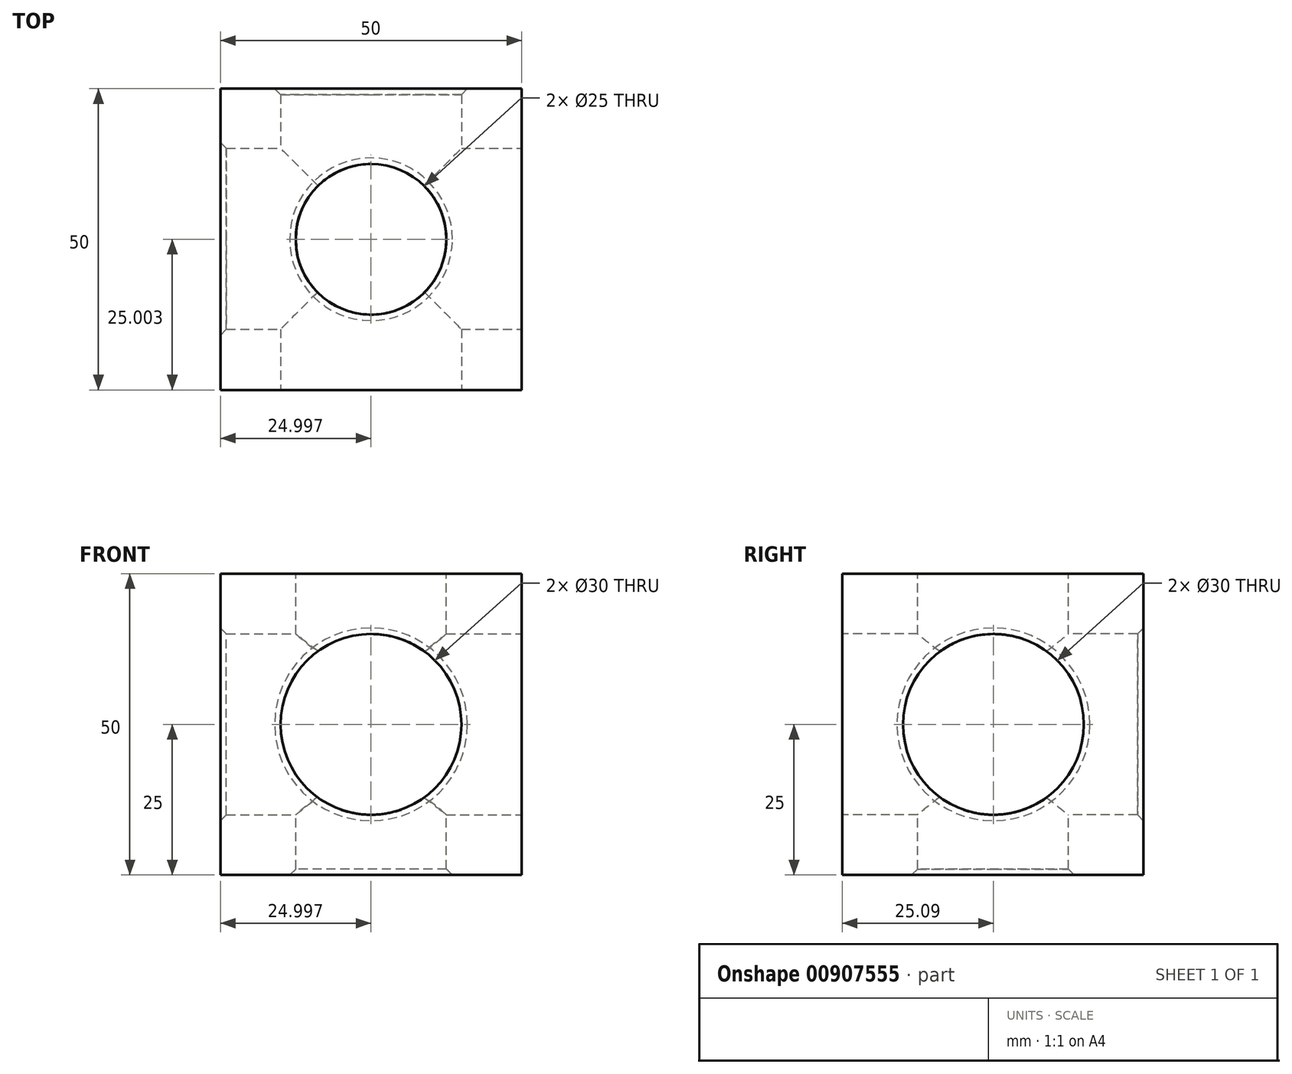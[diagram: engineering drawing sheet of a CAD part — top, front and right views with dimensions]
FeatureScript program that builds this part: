
annotation { "Feature Type Name" : "Feature", "Feature Type Description" : "" }
export const myFeature = defineFeature(function(context is Context, id is Id, definition is map)
    precondition{}
    {
        {
            var Q0;
            Q0=qCreatedBy(makeId("Top.planeOp"),FACE);
            var sketch = newSketch(context, id + "F0", { "sketchPlane" : qUnion([Q0])});
            skLineSegment(sketch, "E0.bottom", {"start": v(-87.73, 24.91) * mm, "end": v(-37.73, 24.91) * mm});
            skLineSegment(sketch, "E0.top", {"start": v(-87.73, -25.09) * mm, "end": v(-37.73, -25.09) * mm});
            skLineSegment(sketch, "E0.left", {"start": v(-87.73, 24.91) * mm, "end": v(-87.73, -25.09) * mm});
            skLineSegment(sketch, "E0.right", {"start": v(-37.73, 24.91) * mm, "end": v(-37.73, -25.09) * mm});
            skSolve(sketch);
        }
        {
            var Q0;
            Q0=makeQuery(id+"F0.imprint","IMPRINT",FACE,{"disambiguationData":[TD([[makeQuery(id+"F0.imprint","IMPRINT",EDGE,{"derivedFrom":sQuery(id+"F0.wireOp",EDGE,"E0.bottom")}),-1.0]])]});
            extrude(context, id + "F1", {"entities" : qUnion([Q0]), "depth" : 50 * mm, "offsetDistance" : 25 * mm});
        }
        {
            var Q0;
            Q0=makeQuery(id+"F1.opExtrude","SWEPT_FACE",FACE,{"disambiguationData":[OSD([sQuery(id+"F0.wireOp",EDGE,"E0.top")])]});
            var sketch = newSketch(context, id + "F2", { "sketchPlane" : qUnion([Q0])});
            skCircle(sketch, "E1", {"center": v(-62.73, 25) * mm, "radius": 15 * mm});
            skPoint(sketch, "E1.centerSnap0", {"position": v(-87.73, 25) * mm});
            skPoint(sketch, "E1.centerSnap1", {"position": v(-62.73, 50) * mm});
            skSolve(sketch);
        }
        {
            var Q0;
            Q0=makeQuery(id+"F2.imprint","IMPRINT",FACE,{"disambiguationData":[TD([[makeQuery(id+"F2.imprint","IMPRINT",EDGE,{"derivedFrom":sQuery(id+"F2.wireOp",EDGE,"E1")}),1.0]])]});
            extrude(context, id + "F3", {"entities" : qUnion([Q0]), "operationType" : NewBodyOperationType.REMOVE, "endBound" : BoundingType.THROUGH_ALL, "oppositeDirection" : true, "depth" : 25 * mm, "offsetDistance" : 25 * mm});
        }
        {
            var Q0;
            Q0=makeQuery(id+"F1.opExtrude","SWEPT_FACE",FACE,{"disambiguationData":[OSD([sQuery(id+"F0.wireOp",EDGE,"E0.right")])]});
            var sketch = newSketch(context, id + "F4", { "sketchPlane" : qUnion([Q0])});
            skCircle(sketch, "E2", {"center": v(0, 25) * mm, "radius": 15 * mm});
            skPoint(sketch, "E2.centerSnap0", {"position": v(-25.09, 25) * mm});
            skSolve(sketch);
        }
        {
            var Q0;
            Q0=makeQuery(id+"F4.imprint","IMPRINT",FACE,{"disambiguationData":[TD([[makeQuery(id+"F4.imprint","IMPRINT",EDGE,{"derivedFrom":sQuery(id+"F4.wireOp",EDGE,"E2")}),1.0]])]});
            extrude(context, id + "F5", {"entities" : qUnion([Q0]), "operationType" : NewBodyOperationType.REMOVE, "endBound" : BoundingType.THROUGH_ALL, "oppositeDirection" : true, "depth" : 25 * mm, "offsetDistance" : 25 * mm});
        }
        {
            var Q0;
            Q0=makeQuery(id+"F1.opExtrude","CAP_FACE",FACE,{"disambiguationData":[OSD([sQuery(id+"F0.wireOp",EDGE,"E0.bottom"),sQuery(id+"F0.wireOp",EDGE,"E0.top"),sQuery(id+"F0.wireOp",EDGE,"E0.left"),sQuery(id+"F0.wireOp",EDGE,"E0.right")])],"isStart":false});
            var sketch = newSketch(context, id + "F6", { "sketchPlane" : qUnion([Q0])});
            skCircle(sketch, "E3", {"center": v(-62.73, -0.09) * mm, "radius": 12.5 * mm});
            skPoint(sketch, "E3.centerSnap0", {"position": v(-62.73, 24.91) * mm});
            skPoint(sketch, "E3.centerSnap1", {"position": v(-37.73, -0.09) * mm});
            skSolve(sketch);
        }
        {
            var Q0;
            Q0=makeQuery(id+"F6.imprint","IMPRINT",FACE,{"disambiguationData":[TD([[makeQuery(id+"F6.imprint","IMPRINT",EDGE,{"derivedFrom":sQuery(id+"F6.wireOp",EDGE,"E3")}),1.0]])]});
            extrude(context, id + "F7", {"entities" : qUnion([Q0]), "operationType" : NewBodyOperationType.REMOVE, "endBound" : BoundingType.THROUGH_ALL, "oppositeDirection" : true, "depth" : 25 * mm, "offsetDistance" : 25 * mm});
        }
        {
            var Q0;
            Q0=makeQuery(id+"F3.boolean.opBoolean","COPY",EDGE,{"derivedFrom":makeQuery(id+"F3.opExtrude","CAP_EDGE",EDGE,{"disambiguationData":[OSD([sQuery(id+"F2.wireOp",EDGE,"E1")])],"isStart":true})});
            var Q1;
            Q1=makeQuery(id+"F5.boolean.opBoolean","COPY",EDGE,{"derivedFrom":makeQuery(id+"F5.opExtrude","CAP_EDGE",EDGE,{"disambiguationData":[OSD([sQuery(id+"F4.wireOp",EDGE,"E2")])],"isStart":true})});
            var Q2;
            Q2=makeQuery(id+"F7.boolean.opBoolean","COPY",EDGE,{"derivedFrom":makeQuery(id+"F7.opExtrude","CAP_EDGE",EDGE,{"disambiguationData":[OSD([sQuery(id+"F6.wireOp",EDGE,"E3")])],"isStart":true})});
            var Q3;
            Q3=makeQuery(id+"F3.boolean.opBoolean","INTERSECT",EDGE,{"derivedFrom":[makeQuery(id+"F1.opExtrude","SWEPT_FACE",FACE,{"disambiguationData":[OSD([sQuery(id+"F0.wireOp",EDGE,"E0.bottom")])]}),makeQuery(id+"F3.opExtrude","SWEPT_FACE",FACE,{"disambiguationData":[OSD([sQuery(id+"F2.wireOp",EDGE,"E1")])]})]});
            var Q4;
            Q4=makeQuery(id+"F7.boolean.opBoolean","INTERSECT",EDGE,{"derivedFrom":[makeQuery(id+"F1.opExtrude","CAP_FACE",FACE,{"disambiguationData":[OSD([sQuery(id+"F0.wireOp",EDGE,"E0.bottom"),sQuery(id+"F0.wireOp",EDGE,"E0.top"),sQuery(id+"F0.wireOp",EDGE,"E0.left"),sQuery(id+"F0.wireOp",EDGE,"E0.right")])],"isStart":true}),makeQuery(id+"F7.opExtrude","SWEPT_FACE",FACE,{"disambiguationData":[OSD([sQuery(id+"F6.wireOp",EDGE,"E3")])]})]});
            var Q5;
            Q5=makeQuery(id+"F5.boolean.opBoolean","INTERSECT",EDGE,{"derivedFrom":[makeQuery(id+"F1.opExtrude","SWEPT_FACE",FACE,{"disambiguationData":[OSD([sQuery(id+"F0.wireOp",EDGE,"E0.left")])]}),makeQuery(id+"F5.opExtrude","SWEPT_FACE",FACE,{"disambiguationData":[OSD([sQuery(id+"F4.wireOp",EDGE,"E2")])]})]});
            chamfer(context, id + "F8", {"entities" : qUnion([Q0, Q1, Q2, Q3, Q4, Q5]), "width" : 1 * mm, "tangentPropagation" : true});
        }
    });
